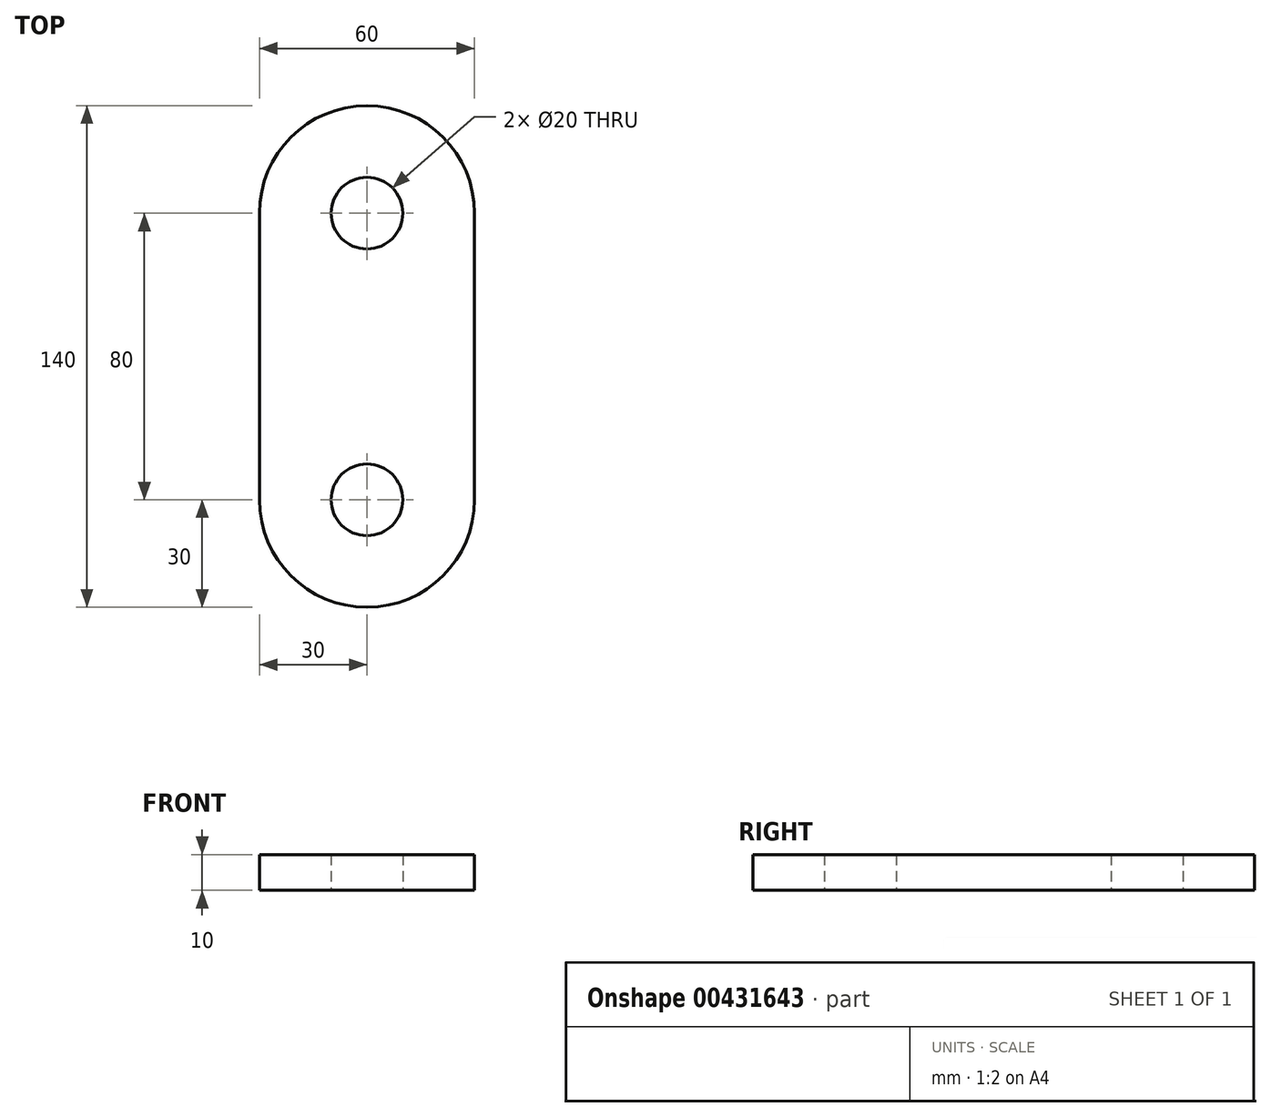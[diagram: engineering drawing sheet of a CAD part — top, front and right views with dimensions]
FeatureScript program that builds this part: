
annotation { "Feature Type Name" : "Feature", "Feature Type Description" : "" }
export const myFeature = defineFeature(function(context is Context, id is Id, definition is map)
    precondition{}
    {
        {
            var Q0;
            Q0=qCreatedBy(makeId("Top.planeOp"),FACE);
            var sketch = newSketch(context, id + "F0", { "sketchPlane" : qUnion([Q0])});
            skLineSegment(sketch, "E0", {"start": v(0, 0) * mm, "end": v(0, -30) * mm, "construction": true});
            skLineSegment(sketch, "E1", {"start": v(0, -30) * mm, "end": v(0, 110) * mm, "construction": true});
            skLineSegment(sketch, "E2", {"start": v(0, 110) * mm, "end": v(0, 80) * mm, "construction": true});
            skLineSegment(sketch, "E3", {"start": v(0, 0) * mm, "end": v(-30, 0) * mm, "construction": true});
            skLineSegment(sketch, "E4", {"start": v(-30, 0) * mm, "end": v(30, 0) * mm, "construction": true});
            skLineSegment(sketch, "E5", {"start": v(0, 80) * mm, "end": v(-30, 80) * mm, "construction": true});
            skLineSegment(sketch, "E6", {"start": v(-30, 80) * mm, "end": v(30, 80) * mm, "construction": true});
            skArc(sketch, "E7", {"start": v(-30, 80) * mm, "mid": v(0, 50) * mm, "end": v(30, 80) * mm, "construction": true});
            skArc(sketch, "E8", {"start": v(30, 80) * mm, "mid": v(0, 110) * mm, "end": v(-30, 80) * mm});
            skArc(sketch, "E9", {"start": v(-30, 0) * mm, "mid": v(0, -30) * mm, "end": v(30, 0) * mm});
            skArc(sketch, "E10", {"start": v(30, 0) * mm, "mid": v(0, 30) * mm, "end": v(-30, 0) * mm, "construction": true});
            skLineSegment(sketch, "E11", {"start": v(-30, 0) * mm, "end": v(-30, 80) * mm});
            skLineSegment(sketch, "E12", {"start": v(30, 80) * mm, "end": v(30, 0) * mm});
            skCircle(sketch, "E13", {"center": v(0, 0) * mm, "radius": 10 * mm});
            skCircle(sketch, "E14", {"center": v(0, 80) * mm, "radius": 10 * mm});
            skSolve(sketch);
        }
        {
            var Q0;
            Q0=makeQuery(id+"F0.imprint","IMPRINT",FACE,{"disambiguationData":[TD([[makeQuery(id+"F0.imprint","IMPRINT",EDGE,{"derivedFrom":sQuery(id+"F0.wireOp",EDGE,"E8")}),1.0]])]});
            extrude(context, id + "F1", {"entities" : qUnion([Q0]), "depth" : 10 * mm});
        }
    });
